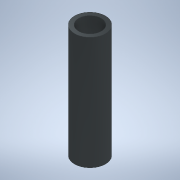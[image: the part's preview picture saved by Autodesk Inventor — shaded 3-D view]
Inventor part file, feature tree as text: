
AUTODESK INVENTOR PART (.ipt)
format: ipt  version: 2020.3 (Build 243373000, 373)  size: 97,280 bytes
history: native  units: mm
features: extrude x1, sketch x1
ambient origin geometry x8: Origin, YZ Plane, XZ Plane, XY Plane, X Axis, Y Axis, Z Axis, Center Point
bodies: Solid1 (feature_tree)
feature tree (2):
  extrude  "Extrusion1"  Depth=10.0mm
  sketch  "Sketch1"  dims[d0=13.6mm d1=10.0mm d2=50.0mm d3=0.0mm]
